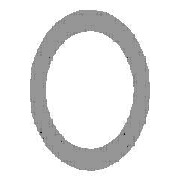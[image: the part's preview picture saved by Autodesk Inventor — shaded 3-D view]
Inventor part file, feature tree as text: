
AUTODESK INVENTOR PART (.ipt)
format: ipt  version: 2013 (Build 170138000, 138)  size: 121,856 bytes
history: native  units: mm (DEFAULTED — no unit token found)
features: other x4, plane x4, sketch x4, extrude x1
ambient origin geometry x8: Origin, YZ Plane, XZ Plane, XY Plane, X Axis, Y Axis, Z Axis, Center Point
bodies: Solid1 (feature_tree), Body (feature_tree)
feature tree (13):
  parser-record x1  (decoder bookkeeping rows leaked as tree rows — omitted from the tree; the rows remain in map.json)
  other  "Driven Length"
  other  "Start plane"
  other  "End plane"
  plane  "Work Plane4"
  plane  "Work Plane5"
  plane  "Work Plane6"
  extrude  "Extrusion2"  Depth=3.3782mm
  sketch  "Sketch"  dims[d5=1473.2mm d6=90.0deg d7=1473.2mm d8=3.302mm d9=0.0mm]
  sketch  "Sketch3"  dims[d0=33.401mm d1=3.3782mm]
  plane  "Work Plane3"
  sketch  "Sketch4"  dims[d2=1473.2mm d3=0.0mm]
  sketch  "Sketch5"  dims[d4=-0.0mm]
